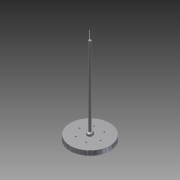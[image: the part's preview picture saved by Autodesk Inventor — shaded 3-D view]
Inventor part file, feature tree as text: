
AUTODESK INVENTOR PART (.ipt)
format: ipt  version: 2012 SP2 (Build 160219200, 219)  size: 187,904 bytes
history: native  units: in
note: dims shown in document units (in); Inventor stores cm internally (conversion verified against a paired STEP export)
features: other x35, extrude x5, sketch x5, pattern_circular x2, plane x1, fillet x1
ambient origin geometry x8: Origin, YZ Plane, XZ Plane, XY Plane, X Axis, Y Axis, Z Axis, Center Point
bodies: Solid1 (feature_tree)
feature tree (49):
  plane  "Work Plane1"
  extrude  "Extrusion1"  Depth=1.378in TaperAngle=0.0deg
  extrude  "Extrusion2"  Depth=0.5906in TaperAngle=0.0deg
  pattern_circular  "Circular Pattern1"  Count=36 Angle=360.0deg
  extrude  "Extrusion3"  Depth=0.7874in
  extrude  "Extrusion4"  Depth=0.4537in
  fillet  "Fillet1"  Radius=3.1496in
  extrude  "Extrusion5"  Depth=27.5591in TaperAngle=0.0deg
  pattern_circular  "Circular Pattern2"  Count=6 Angle=360.0deg
  sketch  "Sketch2"  dims[d2=11.811in d3=1.378in d4=0.0in]
  sketch  "Sketch3"  dims[d5=0.1575in d6=0.5906in d7=0.0in d8=14.1732in d9=360.0deg]
  other  "Work Axis1"
  other  "Work Axis2"
  other  "Work Axis3"
  other  "Work Axis4"
  other  "Work Axis5"
  other  "Work Axis6"
  other  "Work Axis7"
  other  "Work Axis8"
  other  "Work Axis9"
  other  "Work Axis10"
  other  "Work Axis11"
  other  "Work Axis12"
  other  "Work Axis13"
  other  "Work Axis14"
  other  "Work Axis15"
  other  "Work Axis16"
  other  "Work Axis17"
  other  "Work Axis18"
  other  "Work Axis19"
  other  "Work Axis20"
  other  "Work Axis21"
  other  "Work Axis22"
  other  "Work Axis23"
  other  "Work Axis24"
  other  "Work Axis25"
  other  "Work Axis26"
  other  "Work Axis27"
  other  "Work Axis28"
  other  "Work Axis29"
  other  "Work Axis30"
  other  "Work Axis31"
  other  "Work Axis32"
  other  "Work Axis33"
  other  "Work Axis34"
  other  "Work Axis35"
  sketch  "Sketch4"  dims[d11=0.7874in d12=0.0in d13=0.7874in]
  sketch  "Sketch5"  dims[d14=23.622in d15=0.0in d16=0.4537in d17=3.1496in]
  sketch  "Sketch6"  dims[d18=0.3937in d19=27.5591in d20=0.0in d21=2.3622in d22=360.0deg]
